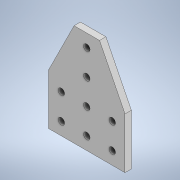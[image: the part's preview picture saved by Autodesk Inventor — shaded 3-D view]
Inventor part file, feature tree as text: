
AUTODESK INVENTOR PART (.ipt)
format: ipt  version: 2020 (Build 240168000, 168)  size: 121,344 bytes
history: native  units: in
note: dims shown in document units (in); Inventor stores cm internally (conversion verified against a paired STEP export)
features: extrude x1, sketch x1
ambient origin geometry x8: Origin, YZ Plane, XZ Plane, XY Plane, X Axis, Y Axis, Z Axis, Center Point
bodies: Solid1 (feature_tree)
feature tree (2):
  extrude  "Extrusion1"  Depth=3.0in
  sketch  "Sketch1"  dims[d10=2.0in d13=3.0in d14=1.0in d15=1.0in d16=2.0in d17=0.256in d18=0.5in d19=0.5in d20=0.7874in d22=1.0in d23=1.1811in d25=1.0in d28=1.1811in d30=1.0in d31=0.3937in d33=1.0in d35=0.25in d36=0.0in]
